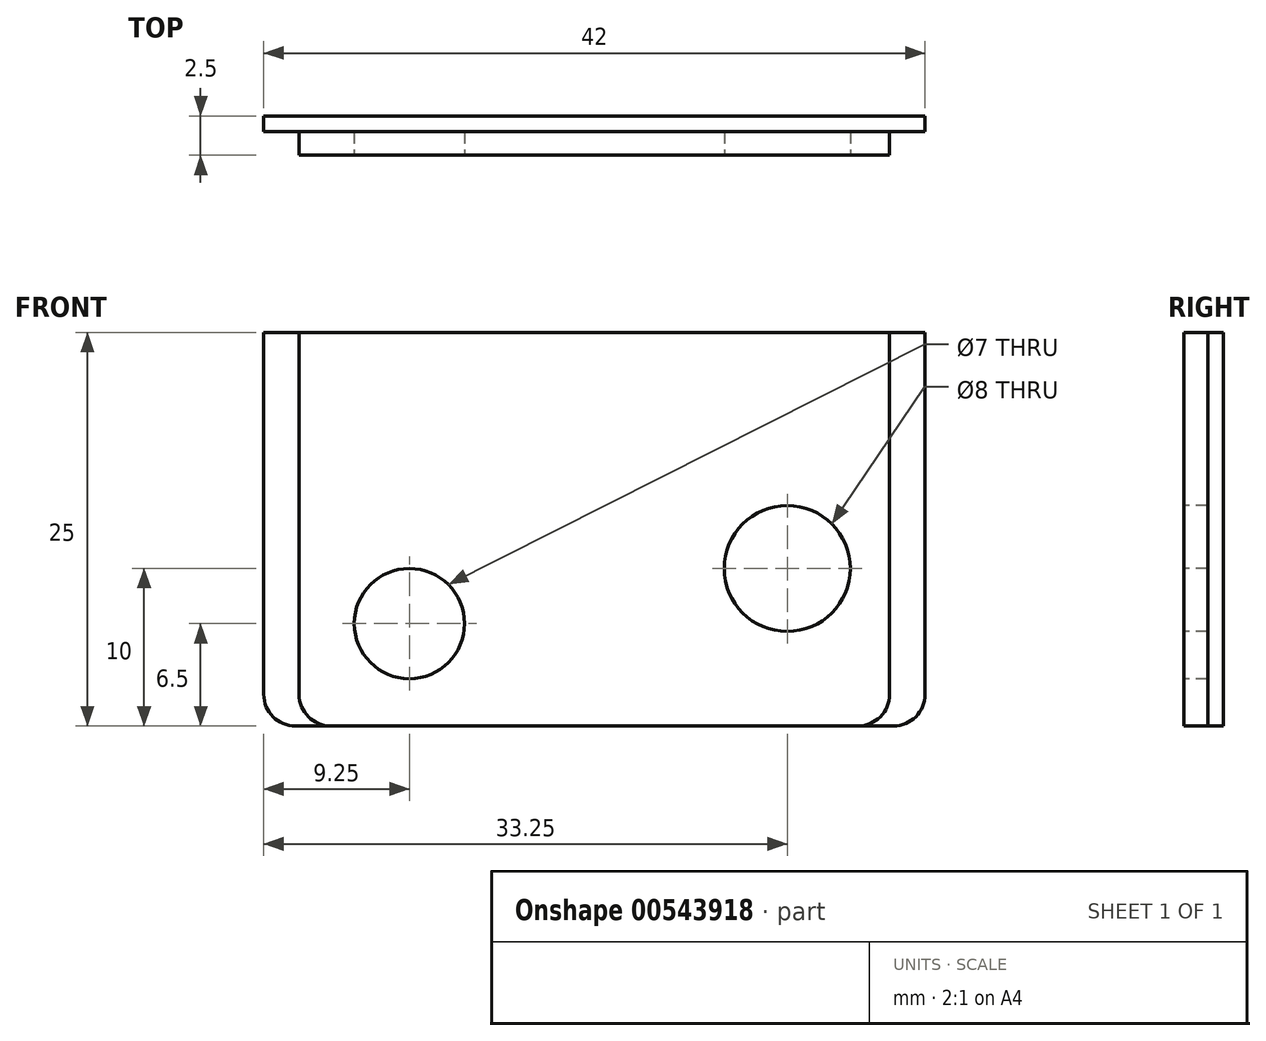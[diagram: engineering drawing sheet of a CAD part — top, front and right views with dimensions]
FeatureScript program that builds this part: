
annotation { "Feature Type Name" : "Feature", "Feature Type Description" : "" }
export const myFeature = defineFeature(function(context is Context, id is Id, definition is map)
    precondition{}
    {
        {
            var Q0;
            Q0=qCreatedBy(makeId("Front.planeOp"),FACE);
            var sketch = newSketch(context, id + "F0", { "sketchPlane" : qUnion([Q0])});
            skLineSegment(sketch, "E0.bottom", {"start": v(2, 0) * mm, "end": v(40, 0) * mm});
            skLineSegment(sketch, "E0.top", {"start": v(0, 25) * mm, "end": v(42, 25) * mm});
            skLineSegment(sketch, "E0.left", {"start": v(0, 2) * mm, "end": v(0, 25) * mm});
            skLineSegment(sketch, "E0.right", {"start": v(42, 2) * mm, "end": v(42, 25) * mm});
            skPoint(sketch, "E1.visualSharp", {"position": v(0, 0) * mm});
            skArc(sketch, "E1.filletArc", {"start": v(0, 2) * mm, "mid": v(0.59, 0.59) * mm, "end": v(2, 0) * mm});
            skPoint(sketch, "E2.visualSharp", {"position": v(42, 0) * mm});
            skArc(sketch, "E2.filletArc", {"start": v(40, 0) * mm, "mid": v(41.41, 0.59) * mm, "end": v(42, 2) * mm});
            skSolve(sketch);
        }
        {
            var Q0;
            Q0=qSketchRegion(id+"F0",true);
            extrude(context, id + "F1", {"entities" : qUnion([Q0]), "depth" : 1 * mm, "offsetDistance" : 25 * mm});
        }
        {
            var Q0;
            Q0=makeQuery(id+"F1.opExtrude","CAP_FACE",FACE,{"disambiguationData":[OSD([sQuery(id+"F0.wireOp",EDGE,"E0.bottom"),sQuery(id+"F0.wireOp",EDGE,"E0.top"),sQuery(id+"F0.wireOp",EDGE,"E0.left"),sQuery(id+"F0.wireOp",EDGE,"E0.right")])],"isStart":false});
            var sketch = newSketch(context, id + "F2", { "sketchPlane" : qUnion([Q0])});
            skLineSegment(sketch, "E3.bottom", {"start": v(2.25, 25) * mm, "end": v(39.75, 25) * mm});
            skLineSegment(sketch, "E3.top", {"start": v(4.25, 0) * mm, "end": v(37.75, 0) * mm});
            skLineSegment(sketch, "E3.left", {"start": v(2.25, 25) * mm, "end": v(2.25, 2) * mm});
            skLineSegment(sketch, "E3.right", {"start": v(39.75, 25) * mm, "end": v(39.75, 2) * mm});
            skPoint(sketch, "E4", {"position": v(21, 25) * mm});
            skPoint(sketch, "E5.visualSharp", {"position": v(2.25, 0) * mm});
            skArc(sketch, "E5.filletArc", {"start": v(2.25, 2) * mm, "mid": v(2.84, 0.59) * mm, "end": v(4.25, 0) * mm});
            skPoint(sketch, "E6.visualSharp", {"position": v(39.75, 0) * mm});
            skArc(sketch, "E6.filletArc", {"start": v(37.75, 0) * mm, "mid": v(39.16, 0.59) * mm, "end": v(39.75, 2) * mm});
            skSolve(sketch);
        }
        {
            var Q0;
            Q0=qSketchRegion(id+"F2",true);
            extrude(context, id + "F3", {"entities" : qUnion([Q0]), "depth" : 1.5 * mm});
        }
        {
            var Q0;
            Q0=makeQuery(id+"F3.opExtrude","CAP_FACE",FACE,{"disambiguationData":[OSD([sQuery(id+"F2.wireOp",EDGE,"E3.bottom"),sQuery(id+"F2.wireOp",EDGE,"E3.top"),sQuery(id+"F2.wireOp",EDGE,"E3.left"),sQuery(id+"F2.wireOp",EDGE,"E3.right"),sQuery(id+"F2.wireOp",EDGE,"E5.filletArc"),sQuery(id+"F2.wireOp",EDGE,"E6.filletArc")])],"isStart":false});
            var sketch = newSketch(context, id + "F4", { "sketchPlane" : qUnion([Q0])});
            skCircle(sketch, "E7", {"center": v(33.25, 10) * mm, "radius": 4 * mm});
            skCircle(sketch, "E8", {"center": v(9.25, 6.5) * mm, "radius": 3.5 * mm});
            skSolve(sketch);
        }
        {
            var Q0;
            Q0 = qSketchRegion(id + "F4", true);
            extrude(context, id + "F5", {"entities" : qUnion([Q0]), "operationType" : NewBodyOperationType.REMOVE, "endBound" : BoundingType.UP_TO_NEXT, "oppositeDirection" : true, "depth" : 25 * mm, "offsetDistance" : 25 * mm});
        }
    });
